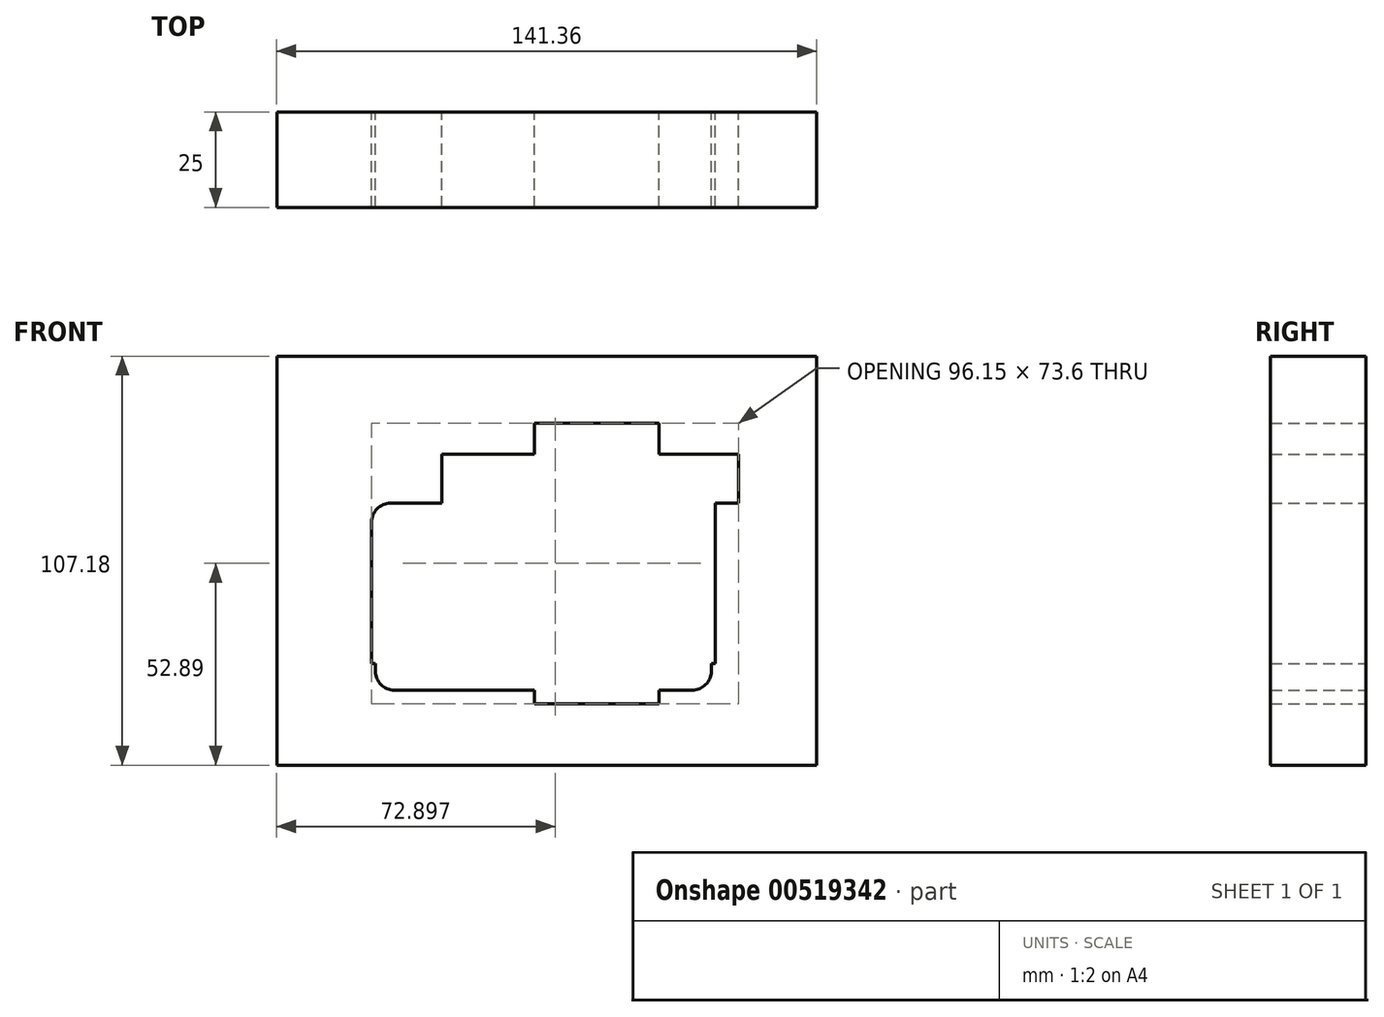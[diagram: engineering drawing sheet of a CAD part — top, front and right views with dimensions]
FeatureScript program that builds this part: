
annotation { "Feature Type Name" : "Feature", "Feature Type Description" : "" }
export const myFeature = defineFeature(function(context is Context, id is Id, definition is map)
    precondition{}
    {
        {
            var Q0;
            Q0=qCreatedBy(makeId("Front.planeOp"),FACE);
            var sketch = newSketch(context, id + "F0", { "sketchPlane" : qUnion([Q0])});
            skLineSegment(sketch, "E0.bottom", {"start": v(0, 0) * mm, "end": v(1, 0) * mm});
            skLineSegment(sketch, "E0.top", {"start": v(5, 42) * mm, "end": v(18.46, 42) * mm});
            skLineSegment(sketch, "E0.left", {"start": v(0, 0) * mm, "end": v(0, 37) * mm});
            skLineSegment(sketch, "E0.right", {"start": v(90, 0) * mm, "end": v(90, 42) * mm});
            skPoint(sketch, "E1.visualSharp", {"position": v(0, 42) * mm});
            skArc(sketch, "E1.filletArc", {"start": v(5, 42) * mm, "mid": v(1.46, 40.54) * mm, "end": v(0, 37) * mm});
            skPoint(sketch, "E2.visualSharp", {"position": v(90, 42) * mm});
            skLineSegment(sketch, "E3", {"start": v(1, 0) * mm, "end": v(1, -2) * mm});
            skLineSegment(sketch, "E4", {"start": v(6, -7) * mm, "end": v(42.63, -7) * mm});
            skLineSegment(sketch, "E5", {"start": v(89, -2) * mm, "end": v(89, 0) * mm});
            skLineSegment(sketch, "E6.trimOffspring", {"start": v(89, 0) * mm, "end": v(90, 0) * mm});
            skPoint(sketch, "E7.visualSharp", {"position": v(1, -7) * mm});
            skArc(sketch, "E7.filletArc", {"start": v(1, -2) * mm, "mid": v(2.46, -5.54) * mm, "end": v(6, -7) * mm});
            skPoint(sketch, "E8.visualSharp", {"position": v(89, -7) * mm});
            skArc(sketch, "E8.filletArc", {"start": v(84, -7) * mm, "mid": v(87.54, -5.54) * mm, "end": v(89, -2) * mm});
            skLineSegment(sketch, "E9", {"start": v(18.46, 42) * mm, "end": v(18.46, 54.86) * mm});
            skLineSegment(sketch, "E10", {"start": v(18.46, 54.86) * mm, "end": v(42.63, 54.86) * mm});
            skLineSegment(sketch, "E11", {"start": v(96.15, 54.86) * mm, "end": v(96.15, 42) * mm});
            skLineSegment(sketch, "E12", {"start": v(96.15, 42) * mm, "end": v(90, 42) * mm});
            skLineSegment(sketch, "E13", {"start": v(42.63, 54.86) * mm, "end": v(42.63, 63.02) * mm});
            skLineSegment(sketch, "E14", {"start": v(42.63, 63.02) * mm, "end": v(75.26, 63.02) * mm});
            skLineSegment(sketch, "E15", {"start": v(75.26, 63.02) * mm, "end": v(75.26, 54.86) * mm});
            skLineSegment(sketch, "E16", {"start": v(42.63, 54.86) * mm, "end": v(42.63, -7) * mm, "construction": true});
            skLineSegment(sketch, "E17", {"start": v(75.26, 54.86) * mm, "end": v(75.26, -7) * mm, "construction": true});
            skLineSegment(sketch, "E18", {"start": v(42.63, -7) * mm, "end": v(42.63, -10.58) * mm});
            skLineSegment(sketch, "E19", {"start": v(42.63, -10.58) * mm, "end": v(75.26, -10.58) * mm});
            skLineSegment(sketch, "E20", {"start": v(75.26, -7) * mm, "end": v(75.26, -10.58) * mm});
            skLineSegment(sketch, "E21.trimOffspring", {"start": v(75.26, 54.86) * mm, "end": v(96.15, 54.86) * mm});
            skLineSegment(sketch, "E22.trimOffspring", {"start": v(75.26, -7) * mm, "end": v(84, -7) * mm});
            skLineSegment(sketch, "E23.bottom", {"start": v(-24.82, 80.51) * mm, "end": v(116.54, 80.51) * mm});
            skLineSegment(sketch, "E23.top", {"start": v(-24.82, -26.67) * mm, "end": v(116.54, -26.67) * mm});
            skLineSegment(sketch, "E23.left", {"start": v(-24.82, 80.51) * mm, "end": v(-24.82, -26.67) * mm});
            skLineSegment(sketch, "E23.right", {"start": v(116.54, 80.51) * mm, "end": v(116.54, -26.67) * mm});
            skSolve(sketch);
        }
        {
            var Q0;
            Q0=makeQuery(id+"F0.imprint","IMPRINT",FACE,{"disambiguationData":[TD([[makeQuery(id+"F0.imprint","IMPRINT",EDGE,{"derivedFrom":sQuery(id+"F0.wireOp",EDGE,"E0.bottom")}),-1.0]])]});
            extrude(context, id + "F1", {"entities" : qUnion([Q0]), "depth" : 25 * mm, "offsetDistance" : 25 * mm});
        }
    });
